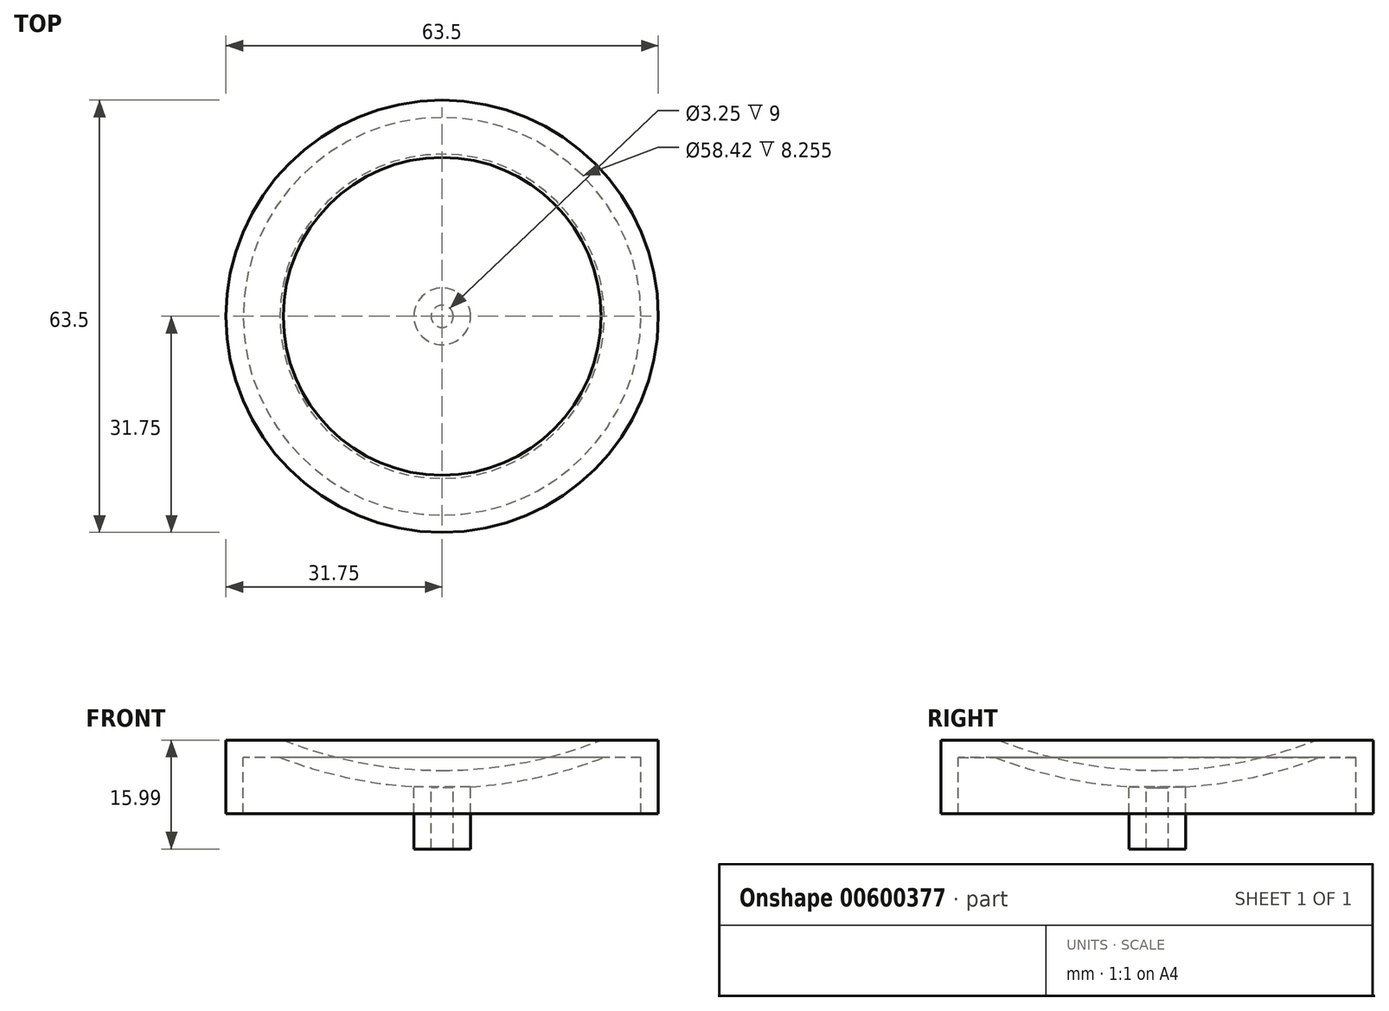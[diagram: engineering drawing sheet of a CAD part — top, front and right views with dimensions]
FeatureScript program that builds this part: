
annotation { "Feature Type Name" : "Feature", "Feature Type Description" : "" }
export const myFeature = defineFeature(function(context is Context, id is Id, definition is map)
    precondition{}
    {
        {
            var Q0;
            Q0=qCreatedBy(makeId("Front.planeOp"),FACE);
            var sketch = newSketch(context, id + "F0", { "sketchPlane" : qUnion([Q0])});
            skCircle(sketch, "E0", {"center": v(0, 59.06) * mm, "radius": 63.5 * mm, "construction": true});
            skLineSegment(sketch, "E1", {"start": v(0, -4.44) * mm, "end": v(0, -6.98) * mm});
            skLineSegment(sketch, "E2", {"start": v(0, -6.98) * mm, "end": v(1.62, -6.98) * mm});
            skLineSegment(sketch, "E3", {"start": v(1.63, -6.99) * mm, "end": v(1.63, -15.98) * mm});
            skLineSegment(sketch, "E4", {"start": v(1.63, -15.98) * mm, "end": v(4.17, -15.98) * mm});
            skLineSegment(sketch, "E5", {"start": v(4.17, -15.98) * mm, "end": v(4.17, -6.85) * mm});
            skLineSegment(sketch, "E6", {"start": v(23.34, 0) * mm, "end": v(31.75, 0) * mm});
            skLineSegment(sketch, "E7", {"start": v(31.75, 0) * mm, "end": v(31.75, -10.8) * mm});
            skLineSegment(sketch, "E8", {"start": v(31.75, -10.8) * mm, "end": v(29.21, -10.8) * mm});
            skLineSegment(sketch, "E9", {"start": v(29.21, -10.8) * mm, "end": v(29.21, -2.54) * mm});
            skLineSegment(sketch, "E10", {"start": v(29.21, -2.54) * mm, "end": v(23.82, -2.54) * mm});
            skArc(sketch, "E11", {"start": v(0, -4.44) * mm, "mid": v(11.88, -3.32) * mm, "end": v(23.34, 0) * mm});
            skArc(sketch, "E12", {"start": v(4.16, -6.85) * mm, "mid": v(14.16, -5.45) * mm, "end": v(23.82, -2.54) * mm});
            skSolve(sketch);
        }
        {
            var Q0;
            Q0=makeQuery(id+"F0.imprint","IMPRINT",FACE,{"disambiguationData":[TD([[makeQuery(id+"F0.imprint","IMPRINT",EDGE,{"derivedFrom":sQuery(id+"F0.wireOp",EDGE,"E1")}),1.0]])]});
            var Q1;
            Q1=sQuery(id+"F0.wireOp",EDGE,"E1");
            revolve(context, id + "F1", {"entities" : qUnion([Q0]), "axis" : qUnion([Q1]), "revolveType" : RevolveType.FULL});
        }
    });
